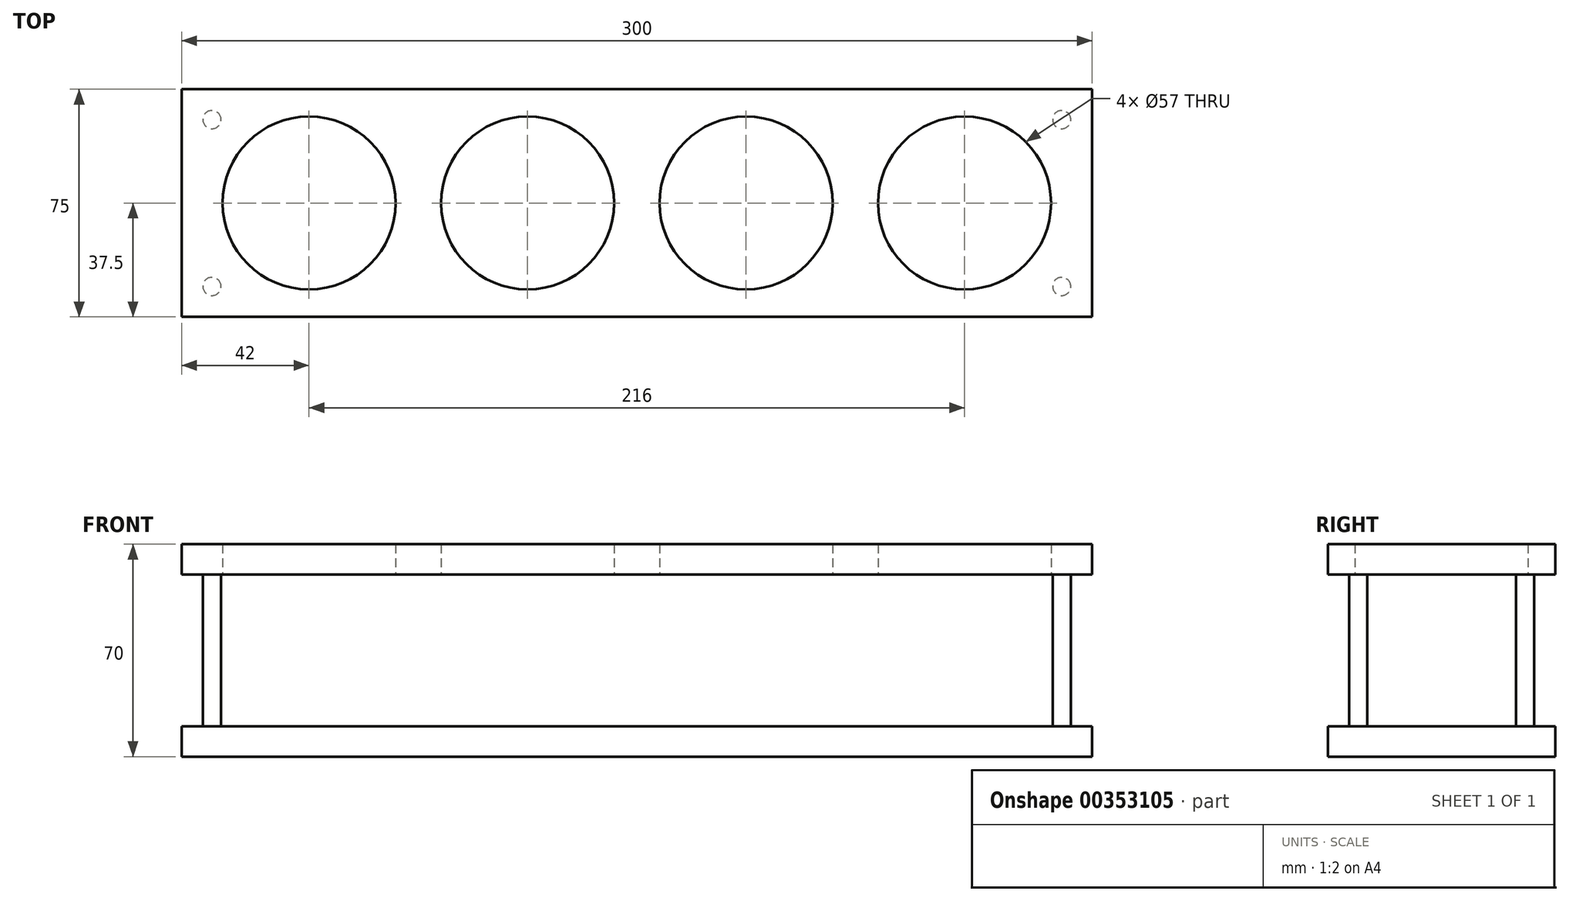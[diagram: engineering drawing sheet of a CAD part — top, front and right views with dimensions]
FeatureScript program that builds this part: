
annotation { "Feature Type Name" : "Feature", "Feature Type Description" : "" }
export const myFeature = defineFeature(function(context is Context, id is Id, definition is map)
    precondition{}
    {
        {
            var Q0;
            Q0=qCreatedBy(makeId("Top.planeOp"),FACE);
            var sketch = newSketch(context, id + "F0", { "sketchPlane" : qUnion([Q0])});
            skLineSegment(sketch, "E0.bottom", {"start": v(150, -37.5) * mm, "end": v(-150, -37.5) * mm});
            skLineSegment(sketch, "E0.top", {"start": v(150, 37.5) * mm, "end": v(-150, 37.5) * mm});
            skLineSegment(sketch, "E0.left", {"start": v(150, -37.5) * mm, "end": v(150, 37.5) * mm});
            skLineSegment(sketch, "E0.right", {"start": v(-150, -37.5) * mm, "end": v(-150, 37.5) * mm});
            skPoint(sketch, "E0.middle", {"position": v(0, 0) * mm});
            skSolve(sketch);
        }
        {
            var Q0;
            Q0 = qSketchRegion(id + "F0", true);
            extrude(context, id + "F1", {"entities" : qUnion([Q0]), "depth" : 10 * mm});
        }
        {
            var Q0;
            Q0=makeQuery(id+"F1.opExtrude","CAP_FACE",FACE,{"disambiguationData":[OSD([sQuery(id+"F0.wireOp",EDGE,"E0.bottom"),sQuery(id+"F0.wireOp",EDGE,"E0.top"),sQuery(id+"F0.wireOp",EDGE,"E0.left"),sQuery(id+"F0.wireOp",EDGE,"E0.right")])],"isStart":false});
            cPlane(context, id + "F2", {"entities" : qUnion([Q0]), "cplaneType" : CPlaneType.OFFSET, "offset" : 50 * mm, "width" : 150 * mm, "height" : 150 * mm});
        }
        {
            var Q0;
            Q0=qCreatedBy(id+"F2.planeOp",FACE);
            var sketch = newSketch(context, id + "F3", { "sketchPlane" : qUnion([Q0])});
            skLineSegment(sketch, "E1.0", {"start": v(150, -37.5) * mm, "end": v(-150, -37.5) * mm});
            skLineSegment(sketch, "E1.1", {"start": v(150, 37.5) * mm, "end": v(-150, 37.5) * mm});
            skLineSegment(sketch, "E1.2", {"start": v(150, -37.5) * mm, "end": v(150, 37.5) * mm});
            skLineSegment(sketch, "E1.3", {"start": v(-150, -37.5) * mm, "end": v(-150, 37.5) * mm});
            skPoint(sketch, "E1.4", {"position": v(0, 0) * mm});
            skLineSegment(sketch, "E2", {"start": v(-150, 0) * mm, "end": v(150, 0) * mm, "construction": true});
            skCircle(sketch, "E3", {"center": v(-108, 0) * mm, "radius": 28.5 * mm});
            skCircle(sketch, "E4.1.0.0", {"center": v(-36, 0) * mm, "radius": 28.5 * mm});
            skCircle(sketch, "E4.2.0.0", {"center": v(36, 0) * mm, "radius": 28.5 * mm});
            skCircle(sketch, "E4.3.0.0", {"center": v(108, 0) * mm, "radius": 28.5 * mm});
            skLineSegment(sketch, "E4.direction1", {"start": v(-108, 0) * mm, "end": v(-36, 0) * mm, "construction": true});
            skSolve(sketch);
        }
        {
            var Q0;
            Q0 = qSketchRegion(id + "F3", true);
            extrude(context, id + "F4", {"entities" : qUnion([Q0]), "depth" : 10 * mm});
        }
        {
            var Q0;
            Q0=makeQuery(id+"F1.opExtrude","CAP_FACE",FACE,{"disambiguationData":[OSD([sQuery(id+"F0.wireOp",EDGE,"E0.bottom"),sQuery(id+"F0.wireOp",EDGE,"E0.top"),sQuery(id+"F0.wireOp",EDGE,"E0.left"),sQuery(id+"F0.wireOp",EDGE,"E0.right")])],"isStart":false});
            var sketch = newSketch(context, id + "F5", { "sketchPlane" : qUnion([Q0])});
            skLineSegment(sketch, "E5", {"start": v(-150, 0) * mm, "end": v(150, 0) * mm, "construction": true});
            skLineSegment(sketch, "E6", {"start": v(150, 0) * mm, "end": v(0, 0) * mm, "construction": true});
            skLineSegment(sketch, "E7", {"start": v(0, 0) * mm, "end": v(0, 37.5) * mm, "construction": true});
            skCircle(sketch, "E8", {"center": v(-140, -27.5) * mm, "radius": 3 * mm});
            skCircle(sketch, "E9.MirrorC", {"center": v(-140, 27.5) * mm, "radius": 3 * mm});
            skCircle(sketch, "E10.MirrorC", {"center": v(140, 27.5) * mm, "radius": 3 * mm});
            skCircle(sketch, "E11.MirrorC", {"center": v(140, -27.5) * mm, "radius": 3 * mm});
            skSolve(sketch);
        }
        {
            var Q0;
            Q0 = qSketchRegion(id + "F5", true);
            var Q1;
            Q1=makeQuery(id+"F4.opExtrude","CAP_FACE",FACE,{"disambiguationData":[OSD([sQuery(id+"F3.wireOp",EDGE,"E1.0"),sQuery(id+"F3.wireOp",EDGE,"E1.1"),sQuery(id+"F3.wireOp",EDGE,"E1.2"),sQuery(id+"F3.wireOp",EDGE,"E1.3"),sQuery(id+"F3.wireOp",EDGE,"E3"),sQuery(id+"F3.wireOp",EDGE,"E4.1.0.0"),sQuery(id+"F3.wireOp",EDGE,"E4.2.0.0"),sQuery(id+"F3.wireOp",EDGE,"E4.3.0.0")])],"isStart":true});
            extrude(context, id + "F6", {"entities" : qUnion([Q0]), "endBound" : BoundingType.UP_TO_SURFACE, "endBoundEntityFace" : qUnion([Q1]), "depth" : 25 * mm});
        }
    });
